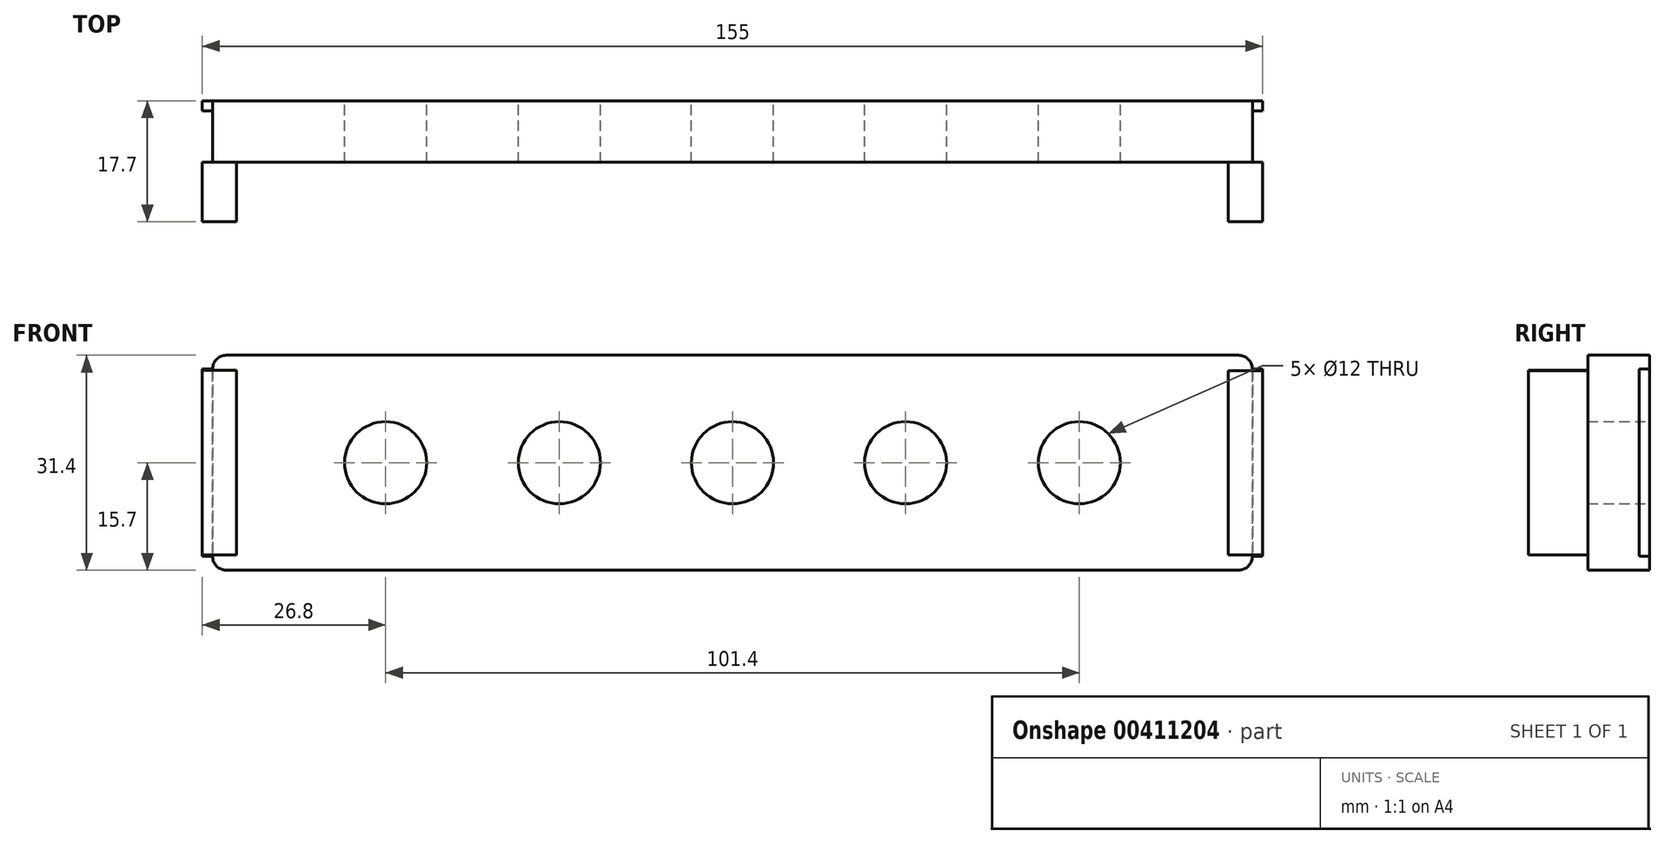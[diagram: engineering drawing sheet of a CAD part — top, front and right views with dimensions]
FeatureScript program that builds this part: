
annotation { "Feature Type Name" : "Feature", "Feature Type Description" : "" }
export const myFeature = defineFeature(function(context is Context, id is Id, definition is map)
    precondition{}
    {
        {
            var Q0;
            Q0=qCreatedBy(makeId("Front.planeOp"),FACE);
            var sketch = newSketch(context, id + "F0", { "sketchPlane" : qUnion([Q0])});
            skLineSegment(sketch, "E0.bottom", {"start": v(76, -15.7) * mm, "end": v(-76, -15.7) * mm});
            skLineSegment(sketch, "E0.top", {"start": v(76, 15.7) * mm, "end": v(-76, 15.7) * mm});
            skLineSegment(sketch, "E0.left", {"start": v(76, -15.7) * mm, "end": v(76, 15.7) * mm});
            skLineSegment(sketch, "E0.right", {"start": v(-76, -15.7) * mm, "end": v(-76, 15.7) * mm});
            skPoint(sketch, "E0.middle", {"position": v(0, 0) * mm});
            skPoint(sketch, "E1", {"position": v(-50.7, 0) * mm});
            skPoint(sketch, "E2", {"position": v(-25.3, 0) * mm});
            skPoint(sketch, "E3", {"position": v(25.3, 0) * mm});
            skPoint(sketch, "E4", {"position": v(50.7, 0) * mm});
            skSolve(sketch);
        }
        {
            var Q0;
            Q0=makeQuery(id+"F0.imprint","IMPRINT",FACE,{"disambiguationData":[TD([[makeQuery(id+"F0.imprint","IMPRINT",EDGE,{"derivedFrom":sQuery(id+"F0.wireOp",EDGE,"E0.bottom")}),-1.0]])]});
            extrude(context, id + "F1", {"entities" : qUnion([Q0]), "depth" : 9 * mm});
        }
        {
            var Q0;
            Q0=makeQuery(id+"F1.opExtrude","SWEPT_EDGE",EDGE,{"disambiguationData":[OSD([sQuery(id+"F0.wireOp",EDGE,"E0.top"),sQuery(id+"F0.wireOp",EDGE,"E0.left")])]});
            var Q1;
            Q1=makeQuery(id+"F1.opExtrude","SWEPT_EDGE",EDGE,{"disambiguationData":[OSD([sQuery(id+"F0.wireOp",EDGE,"E0.bottom"),sQuery(id+"F0.wireOp",EDGE,"E0.left")])]});
            var Q2;
            Q2=makeQuery(id+"F1.opExtrude","SWEPT_EDGE",EDGE,{"disambiguationData":[OSD([sQuery(id+"F0.wireOp",EDGE,"E0.bottom"),sQuery(id+"F0.wireOp",EDGE,"E0.right")])]});
            var Q3;
            Q3=makeQuery(id+"F1.opExtrude","SWEPT_EDGE",EDGE,{"disambiguationData":[OSD([sQuery(id+"F0.wireOp",EDGE,"E0.top"),sQuery(id+"F0.wireOp",EDGE,"E0.right")])]});
            fillet(context, id + "F2", {"entities" : qUnion([Q0, Q1, Q2, Q3]), "radius" : 2 * mm, "tangentPropagation" : true, "allowEdgeOverflow" : false});
        }
        {
            var Q0;
            Q0=makeQuery(id+"F1.opExtrude","CAP_FACE",FACE,{"disambiguationData":[OSD([sQuery(id+"F0.wireOp",EDGE,"E0.bottom"),sQuery(id+"F0.wireOp",EDGE,"E0.top"),sQuery(id+"F0.wireOp",EDGE,"E0.left"),sQuery(id+"F0.wireOp",EDGE,"E0.right")])],"isStart":false});
            var sketch = newSketch(context, id + "F3", { "sketchPlane" : qUnion([Q0])});
            skLineSegment(sketch, "E5.bottom", {"start": v(-72.5, -13.48) * mm, "end": v(-75.5, -13.48) * mm});
            skLineSegment(sketch, "E5.top", {"start": v(-72.5, 13.48) * mm, "end": v(-75.5, 13.48) * mm});
            skLineSegment(sketch, "E5.left", {"start": v(-72.5, -13.48) * mm, "end": v(-72.5, 13.48) * mm});
            skLineSegment(sketch, "E5.right", {"start": v(-75.5, -13.48) * mm, "end": v(-75.5, 13.48) * mm});
            skPoint(sketch, "E5.middle", {"position": v(-74, 0) * mm});
            skLineSegment(sketch, "E6.bottom", {"start": v(75.5, -13.5) * mm, "end": v(72.5, -13.5) * mm});
            skLineSegment(sketch, "E6.top", {"start": v(75.5, 13.45) * mm, "end": v(72.5, 13.45) * mm});
            skLineSegment(sketch, "E6.left", {"start": v(75.5, -13.5) * mm, "end": v(75.5, 13.45) * mm});
            skLineSegment(sketch, "E6.right", {"start": v(72.5, -13.5) * mm, "end": v(72.5, 13.45) * mm});
            skPoint(sketch, "E6.middle", {"position": v(74, -0.02) * mm});
            skSolve(sketch);
        }
        {
            var Q0;
            Q0=makeQuery(id+"F3.imprint","IMPRINT",FACE,{"disambiguationData":[TD([[makeQuery(id+"F3.imprint","IMPRINT",EDGE,{"derivedFrom":sQuery(id+"F3.wireOp",EDGE,"E5.bottom")}),-1.0]])]});
            var Q1;
            Q1=makeQuery(id+"F3.imprint","IMPRINT",FACE,{"disambiguationData":[TD([[makeQuery(id+"F3.imprint","IMPRINT",EDGE,{"derivedFrom":sQuery(id+"F3.wireOp",EDGE,"E6.bottom")}),-1.0]])]});
            extrude(context, id + "F4", {"entities" : qUnion([Q0, Q1]), "operationType" : NewBodyOperationType.ADD, "depth" : 8.7 * mm});
        }
        {
            var Q0;
            Q0=makeQuery(id+"F4.opExtrude","SWEPT_FACE",FACE,{"disambiguationData":[OSD([sQuery(id+"F3.wireOp",EDGE,"E5.right")])]});
            extrude(context, id + "F5", {"entities" : qUnion([Q0]), "operationType" : NewBodyOperationType.ADD, "depth" : 2 * mm});
        }
        {
            var Q0;
            Q0=makeQuery(id+"F4.opExtrude","SWEPT_FACE",FACE,{"disambiguationData":[OSD([sQuery(id+"F3.wireOp",EDGE,"E6.left")])]});
            extrude(context, id + "F6", {"entities" : qUnion([Q0]), "operationType" : NewBodyOperationType.ADD, "depth" : 2 * mm});
        }
        {
            var Q0;
            Q0=makeQuery(id+"F1.opExtrude","SWEPT_FACE",FACE,{"disambiguationData":[OSD([sQuery(id+"F0.wireOp",EDGE,"E0.right")])]});
            var sketch = newSketch(context, id + "F7", { "sketchPlane" : qUnion([Q0])});
            skLineSegment(sketch, "E7.bottom", {"start": v(0, 13.7) * mm, "end": v(1.5, 13.7) * mm});
            skLineSegment(sketch, "E7.top", {"start": v(0, -13.7) * mm, "end": v(1.5, -13.7) * mm});
            skLineSegment(sketch, "E7.left", {"start": v(0, 13.7) * mm, "end": v(0, -13.7) * mm});
            skLineSegment(sketch, "E7.right", {"start": v(1.5, 13.7) * mm, "end": v(1.5, -13.7) * mm});
            skSolve(sketch);
        }
        {
            var Q0;
            Q0=makeQuery(id+"F7.imprint","IMPRINT",FACE,{"disambiguationData":[TD([[makeQuery(id+"F7.imprint","IMPRINT",EDGE,{"derivedFrom":sQuery(id+"F7.wireOp",EDGE,"E7.bottom")}),1.0]])]});
            extrude(context, id + "F8", {"entities" : qUnion([Q0]), "operationType" : NewBodyOperationType.ADD, "depth" : 1.5 * mm});
        }
        {
            var Q0;
            Q0=makeQuery(id+"F1.opExtrude","SWEPT_FACE",FACE,{"disambiguationData":[OSD([sQuery(id+"F0.wireOp",EDGE,"E0.left")])]});
            var sketch = newSketch(context, id + "F9", { "sketchPlane" : qUnion([Q0])});
            skLineSegment(sketch, "E8.bottom", {"start": v(0, 13.7) * mm, "end": v(-1.5, 13.7) * mm});
            skLineSegment(sketch, "E8.top", {"start": v(0, -13.7) * mm, "end": v(-1.5, -13.7) * mm});
            skLineSegment(sketch, "E8.left", {"start": v(0, 13.7) * mm, "end": v(0, -13.7) * mm});
            skLineSegment(sketch, "E8.right", {"start": v(-1.5, 13.7) * mm, "end": v(-1.5, -13.7) * mm});
            skSolve(sketch);
        }
        {
            var Q0;
            Q0=makeQuery(id+"F9.imprint","IMPRINT",FACE,{"disambiguationData":[TD([[makeQuery(id+"F9.imprint","IMPRINT",EDGE,{"derivedFrom":sQuery(id+"F9.wireOp",EDGE,"E8.bottom")}),1.0]])]});
            extrude(context, id + "F10", {"entities" : qUnion([Q0]), "operationType" : NewBodyOperationType.ADD, "depth" : 1.5 * mm});
        }
        {
            var Q0;
            Q0=sQuery(id+"F0.wireOp",VERTEX,"E1");
            var Q1;
            Q1=sQuery(id+"F0.wireOp",VERTEX,"E2");
            var Q2;
            Q2=sQuery(id+"F0.wireOp",VERTEX,"E3");
            var Q3;
            Q3=sQuery(id+"F0.wireOp",VERTEX,"E0.middle");
            var Q4;
            Q4=sQuery(id+"F0.wireOp",VERTEX,"E4");
            var Q5;
            Q5=makeQuery(id+"F1.opExtrude","SWEPT_BODY",BODY,{"disambiguationData":[OSD([sQuery(id+"F0.wireOp",EDGE,"E0.bottom"),sQuery(id+"F0.wireOp",EDGE,"E0.top"),sQuery(id+"F0.wireOp",EDGE,"E0.left"),sQuery(id+"F0.wireOp",EDGE,"E0.right")])]});
            hole(context, id + "F11", {"style" : HoleStyle.SIMPLE, "endStyle" : HoleEndStyle.BLIND, "oppositeDirection" : true, "holeDiameter" : 12 * mm, "holeDepth" : 10 * mm, "isTappedThrough" : true, "tappedDepth" : 12 * mm, "tapClearance" : 3, "locations" : qUnion([Q0, Q1, Q2, Q3, Q4]), "scope" : qUnion([Q5])});
        }
    });
